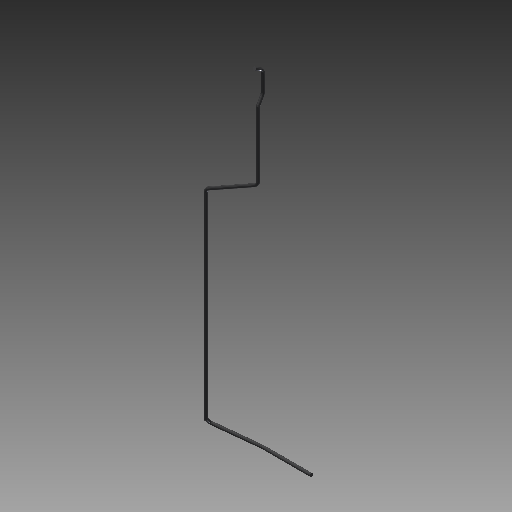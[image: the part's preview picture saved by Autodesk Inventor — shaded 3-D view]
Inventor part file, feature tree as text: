
AUTODESK INVENTOR PART (.ipt)
format: ipt  version: 2019 (Build 230136000, 136)  size: 158,208 bytes
history: native  units: mm
features: sketch x10, plane x7, sweep x5, other x5
ambient origin geometry x8: Origin, YZ Plane, XZ Plane, XY Plane, X Axis, Y Axis, Z Axis, Center Point
bodies: Solid1 (feature_tree)
feature tree (27):
  sketch  "Sketch3"  dims[d0=193.0mm d1=43.0mm]
  plane  "Work Plane1"
  sweep  "Sweep1"
  plane  "Work Plane2"
  sweep  "Sweep2"
  other  "Work Axis8"
  plane  "Work Plane3"
  sweep  "Sweep3"
  plane  "Work Plane4"
  sweep  "Sweep4"
  plane  "Work Plane5"
  sweep  "Sweep5"
  other  "Work Axis11"
  plane  "Work Plane6"
  plane  "Work Plane7"
  sketch  "Sketch4"  dims[d2=99.0mm d3=76.5mm]
  other  "Work Axis7"
  sketch  "Sketch5"  dims[d4=290.0mm d5=8.0mm]
  sketch  "Sketch6"  dims[d6=4.5mm d7=0.0mm]
  sketch  "Sketch7"  dims[d8=0.0mm d10=4.0mm]
  sketch  "Sketch8"  dims[d11=60.0deg]
  other  "Work Axis9"
  sketch  "Sketch9"  dims[d12=7.0mm]
  sketch  "Sketch10"  dims[d13=60.0deg]
  other  "Work Axis10"
  sketch  "Sketch12"  dims[d14=30.5mm]
  sketch  "Sketch13"  dims[d15=14.5mm d16=8.0mm d17=0.0mm d19=8.0mm d21=6.0mm d22=8.726646mm d23=0.0mm d24=90.0deg d25=4.0mm d26=3.316126mm d31=0.0mm d34=1.745329mm d38=3.036873mm d39=4.0mm d40=70.0mm d41=11.082841mm d42=0.0mm d43=0.0mm d44=90.0deg d45=0.0mm d46=0.0mm d47=0.0mm d48=0.0mm d49=0.0mm]
